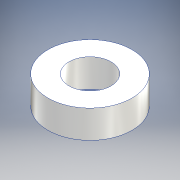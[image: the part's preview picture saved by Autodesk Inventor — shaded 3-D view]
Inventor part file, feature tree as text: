
AUTODESK INVENTOR PART (.ipt)
format: ipt  version: 2016 (Build 200138000, 138)  size: 104,960 bytes
history: native  units: mm
features: other x1, extrude x1, sketch x1
ambient origin geometry x8: Origin, YZ Plane, XZ Plane, XY Plane, X Axis, Y Axis, Z Axis, Center Point
bodies: Body1 (feature_tree)
feature tree (3):
  other  "ソリッド1"
  extrude  "押し出し1"  Depth=6.0mm
  sketch  "スケッチ1"
